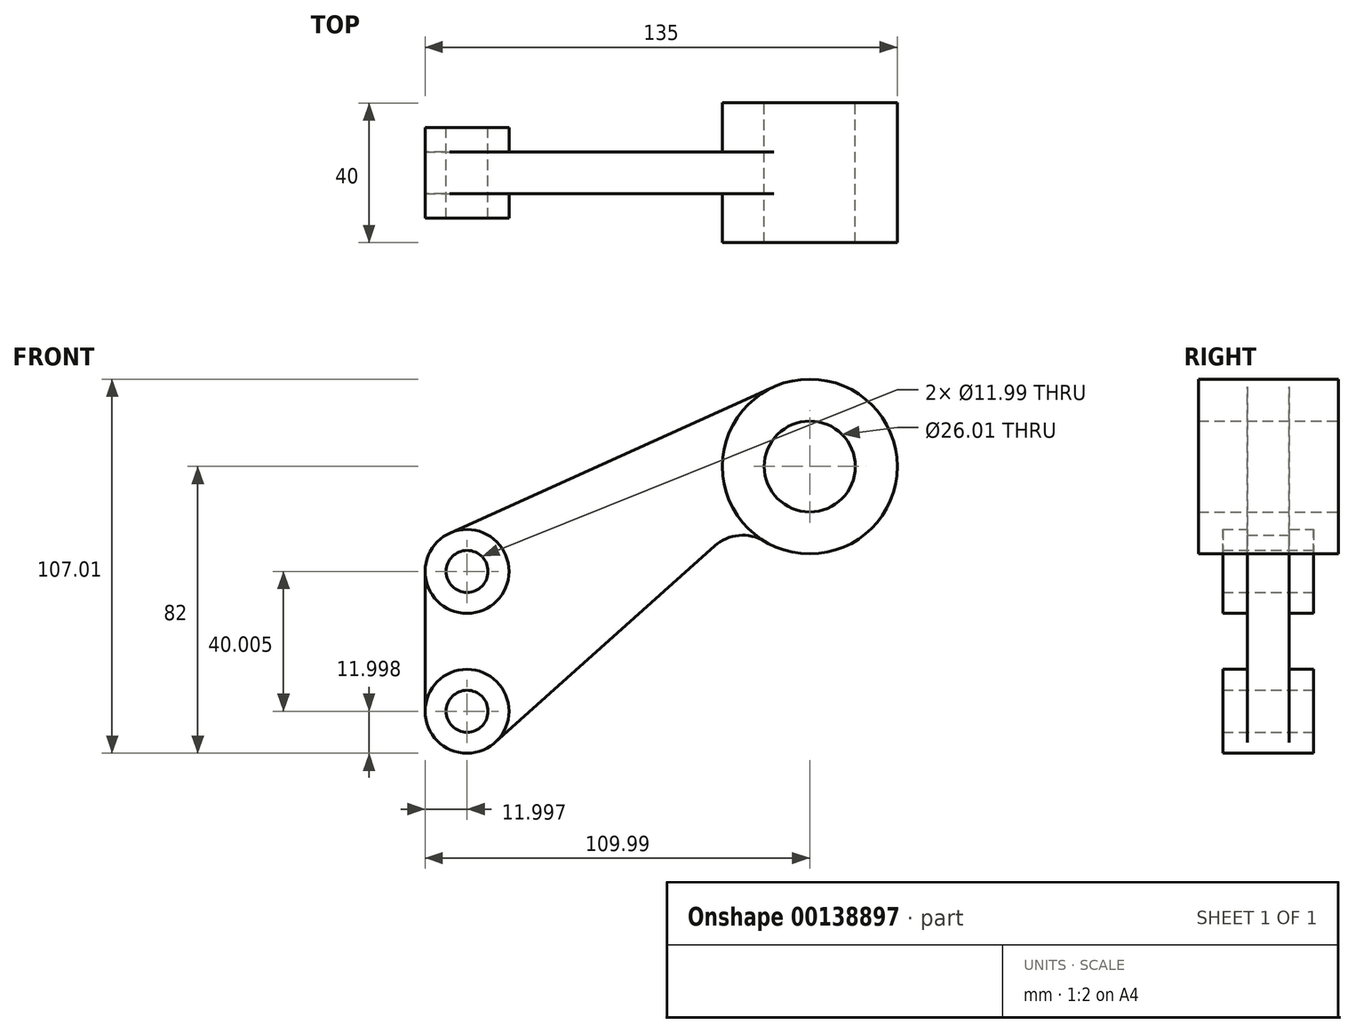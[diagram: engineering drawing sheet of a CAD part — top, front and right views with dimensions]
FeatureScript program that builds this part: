
annotation { "Feature Type Name" : "Feature", "Feature Type Description" : "" }
export const myFeature = defineFeature(function(context is Context, id is Id, definition is map)
    precondition{}
    {
        {
            var Q0;
            Q0=qCreatedBy(makeId("Front.planeOp"),FACE);
            var sketch = newSketch(context, id + "F0", { "sketchPlane" : qUnion([Q0])});
            skCircle(sketch, "E0", {"center": v(0, 0) * mm, "radius": 25 * mm});
            skCircle(sketch, "E1", {"center": v(-98, -30) * mm, "radius": 12 * mm});
            skCircle(sketch, "E2", {"center": v(-98, -70) * mm, "radius": 12 * mm});
            skCircle(sketch, "E3", {"center": v(-98, -30) * mm, "radius": 6 * mm});
            skCircle(sketch, "E4", {"center": v(-98, -70) * mm, "radius": 6 * mm});
            skCircle(sketch, "E5", {"center": v(0, 0) * mm, "radius": 13 * mm});
            skLineSegment(sketch, "E6", {"start": v(-102.93, -19.06) * mm, "end": v(-10.3, 22.79) * mm});
            skLineSegment(sketch, "E7", {"start": v(-110, -70) * mm, "end": v(-110, -30) * mm});
            skPoint(sketch, "E8", {"position": v(-19.16, -31.65) * mm});
            skLineSegment(sketch, "E9", {"start": v(-90, -78.95) * mm, "end": v(-27.15, -22.71) * mm});
            skArc(sketch, "E10", {"start": v(-12.95, -21.4) * mm, "mid": v(-20.27, -19.71) * mm, "end": v(-27.15, -22.71) * mm});
            skSolve(sketch);
        }
        {
            var Q0;
            {var subQ0=sQuery(id+"F0.wireOp",EDGE,"E6");Q0=makeQuery(id+"F0.imprint","IMPRINT",FACE,{"disambiguationData":[TD([[makeQuery(id+"F0.imprint","IMPRINT",EDGE,{"derivedFrom":subQ0}),-1.0]])]});}
            extrude(context, id + "F1", {"entities" : qUnion([Q0]), "endBound" : BoundingType.SYMMETRIC, "depth" : 12 * mm});
        }
        {
            var Q0;
            Q0=makeQuery(id+"F0.imprint","IMPRINT",FACE,{"disambiguationData":[TD([[makeQuery(id+"F0.imprint","IMPRINT",EDGE,{"derivedFrom":sQuery(id+"F0.wireOp",EDGE,"E5")}),-1.0]])]});
            extrude(context, id + "F2", {"entities" : qUnion([Q0]), "operationType" : NewBodyOperationType.ADD, "endBound" : BoundingType.SYMMETRIC, "depth" : 40 * mm});
        }
        {
            var Q0;
            Q0=makeQuery(id+"F0.imprint","IMPRINT",FACE,{"disambiguationData":[TD([[makeQuery(id+"F0.imprint","IMPRINT",EDGE,{"derivedFrom":sQuery(id+"F0.wireOp",EDGE,"E3")}),-1.0]])]});
            var Q1;
            Q1=makeQuery(id+"F0.imprint","IMPRINT",FACE,{"disambiguationData":[TD([[makeQuery(id+"F0.imprint","IMPRINT",EDGE,{"derivedFrom":sQuery(id+"F0.wireOp",EDGE,"E4")}),-1.0]])]});
            extrude(context, id + "F3", {"entities" : qUnion([Q0, Q1]), "operationType" : NewBodyOperationType.ADD, "endBound" : BoundingType.SYMMETRIC, "depth" : 26 * mm});
        }
    });
